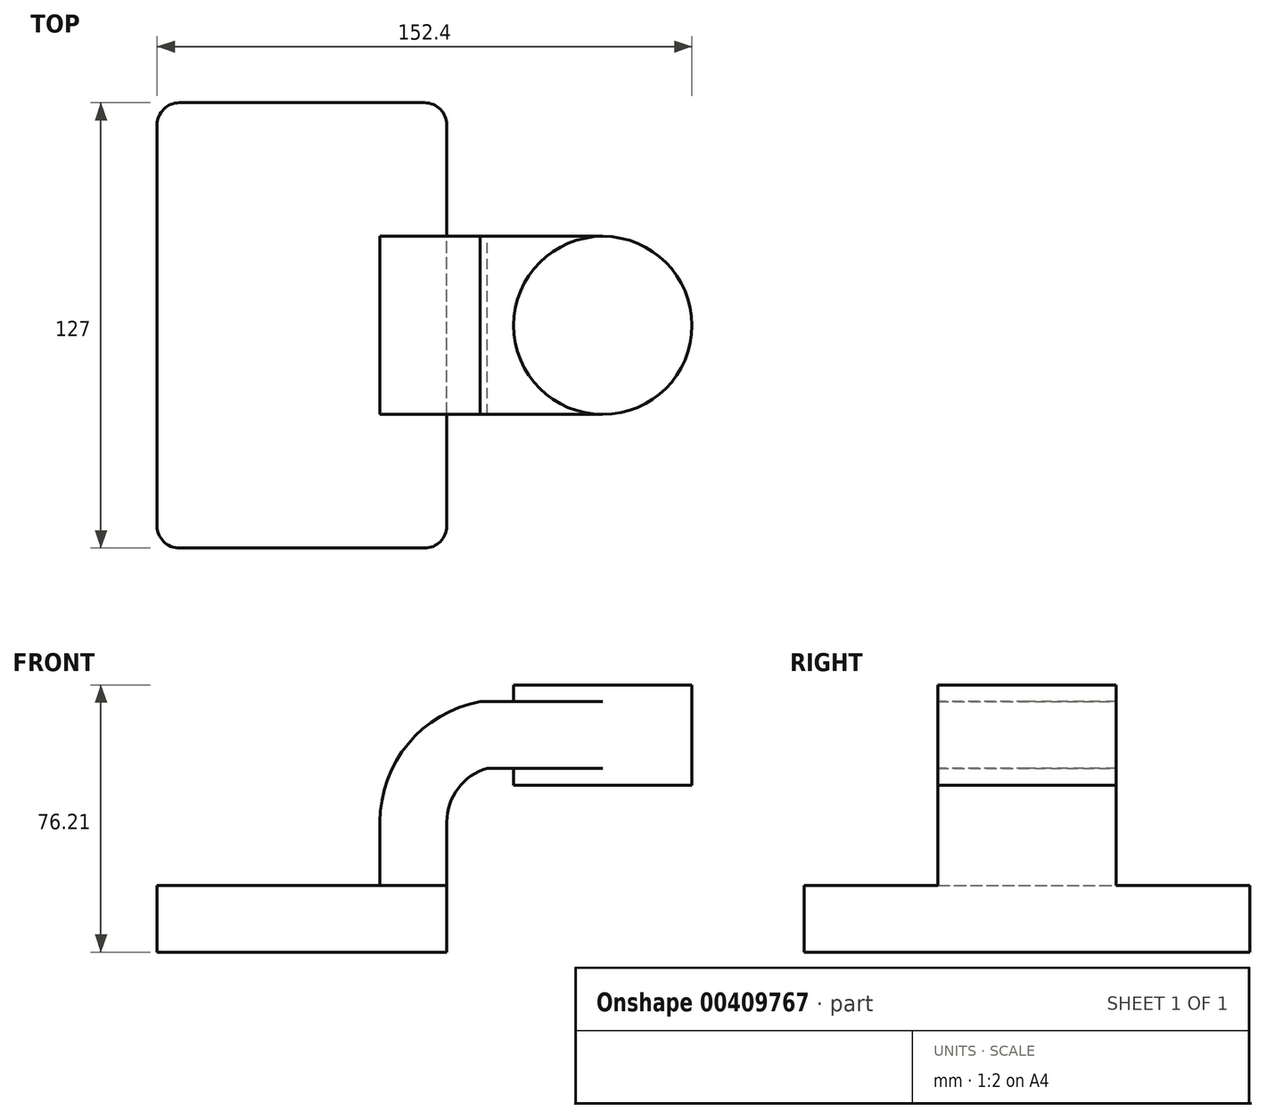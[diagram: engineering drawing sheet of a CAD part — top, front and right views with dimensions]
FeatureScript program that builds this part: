
annotation { "Feature Type Name" : "Feature", "Feature Type Description" : "" }
export const myFeature = defineFeature(function(context is Context, id is Id, definition is map)
    precondition{}
    {
        {
            var Q0;
            Q0=qCreatedBy(makeId("Front.planeOp"),FACE);
            var sketch = newSketch(context, id + "F0", { "sketchPlane" : qUnion([Q0])});
            skLineSegment(sketch, "E0.bottom", {"start": v(41.28, -9.52) * mm, "end": v(-41.28, -9.53) * mm});
            skLineSegment(sketch, "E0.top", {"start": v(41.28, 9.53) * mm, "end": v(-41.28, 9.53) * mm});
            skLineSegment(sketch, "E0.left", {"start": v(41.28, -9.52) * mm, "end": v(41.28, 9.53) * mm});
            skLineSegment(sketch, "E0.right", {"start": v(-41.28, -9.53) * mm, "end": v(-41.28, 9.53) * mm});
            skPoint(sketch, "E0.middle", {"position": v(0, 0) * mm});
            skLineSegment(sketch, "E1.bottom", {"start": v(111.13, 38.1) * mm, "end": v(60.33, 38.1) * mm});
            skLineSegment(sketch, "E1.top", {"start": v(111.13, 66.68) * mm, "end": v(60.33, 66.68) * mm});
            skLineSegment(sketch, "E1.left", {"start": v(111.13, 38.1) * mm, "end": v(111.13, 66.68) * mm});
            skLineSegment(sketch, "E1.right", {"start": v(60.33, 38.1) * mm, "end": v(60.33, 66.68) * mm});
            skPoint(sketch, "E1.middle", {"position": v(85.73, 52.39) * mm});
            skPoint(sketch, "E2.middle", {"position": v(41.28, 9.53) * mm});
            skLineSegment(sketch, "E3", {"start": v(41.28, 9.53) * mm, "end": v(41.28, 27.6) * mm});
            skArc(sketch, "E4", {"start": v(41.27, 27.6) * mm, "mid": v(44.5, 37.18) * mm, "end": v(52.85, 42.88) * mm});
            skLineSegment(sketch, "E5", {"start": v(52.85, 42.88) * mm, "end": v(85.73, 42.88) * mm});
            skLineSegment(sketch, "E6.0", {"start": v(50.74, 61.93) * mm, "end": v(85.73, 61.93) * mm});
            skArc(sketch, "E6.1", {"start": v(22.23, 27.6) * mm, "mid": v(30.28, 49.9) * mm, "end": v(50.74, 61.93) * mm});
            skLineSegment(sketch, "E6.2", {"start": v(22.22, 9.53) * mm, "end": v(22.22, 27.6) * mm});
            skLineSegment(sketch, "E7", {"start": v(85.73, 38.1) * mm, "end": v(85.73, 66.68) * mm});
            skFitSpline(sketch, "E8", {"points": [v(-41.28, 9.52) * mm, v(50.74, 61.93) * mm], "startDerivative": vector(-0.36, 89.6) * mm, "endDerivative": vector(110.06, -0.13) * mm});
            skSolve(sketch);
        }
        {
            var Q0;
            Q0=makeQuery(id+"F0.imprint","IMPRINT",FACE,{"disambiguationData":[TD([[makeQuery(id+"F0.imprint","IMPRINT",EDGE,{"derivedFrom":sQuery(id+"F0.wireOp",EDGE,"E0.bottom")}),-1.0]])]});
            extrude(context, id + "F1", {"entities" : qUnion([Q0]), "endBound" : BoundingType.SYMMETRIC, "depth" : 127 * mm});
        }
        {
            var Q0;
            {var subQ1=sQuery(id+"F0.wireOp",EDGE,"E3");Q0=makeQuery(id+"F0.imprint","IMPRINT",FACE,{"disambiguationData":[TD([[makeQuery(id+"F0.imprint","IMPRINT",EDGE,{"derivedFrom":subQ1}),1.0]])]});}
            var Q1;
            {var subQ0=sQuery(id+"F0.wireOp",EDGE,"E5");var subQ1=sQuery(id+"F0.wireOp",EDGE,"E1.right");var subQ2=makeQuery(id+"F0.imprint","INTERSECT",VERTEX,{"derivedFrom":[subQ1,subQ0]});Q1=makeQuery(id+"F0.imprint","IMPRINT",FACE,{"disambiguationData":[TD([[makeQuery(id+"F0.imprint","IMPRINT",EDGE,{"disambiguationData":[TD([[subQ2,-1.0]])],"derivedFrom":subQ1}),-1.0]])]});}
            extrude(context, id + "F2", {"entities" : qUnion([Q0, Q1]), "operationType" : NewBodyOperationType.ADD, "endBound" : BoundingType.SYMMETRIC, "depth" : 50.8 * mm});
        }
        {
            var Q0;
            Q0=makeQuery(id+"F0.imprint","IMPRINT",FACE,{"disambiguationData":[TD([[makeQuery(id+"F0.imprint","IMPRINT",EDGE,{"derivedFrom":sQuery(id+"F0.wireOp",EDGE,"E6.1")}),1.0]])]});
            extrude(context, id + "F3", {"entities" : qUnion([Q0]), "operationType" : NewBodyOperationType.ADD, "endBound" : BoundingType.SYMMETRIC, "depth" : 15.88 * mm});
        }
        {
            var Q0;
            {var subQ4=sQuery(id+"F0.wireOp",EDGE,"E1.left");Q0=makeQuery(id+"F0.imprint","IMPRINT",FACE,{"disambiguationData":[TD([[makeQuery(id+"F0.imprint","IMPRINT",EDGE,{"derivedFrom":subQ4}),1.0]])]});}
            var Q1;
            Q1=sQuery(id+"F0.wireOp",EDGE,"E7");
            revolve(context, id + "F4", {"operationType" : NewBodyOperationType.ADD, "entities" : qUnion([Q0]), "axis" : qUnion([Q1]), "revolveType" : RevolveType.FULL});
        }
        {
            var Q0;
            Q0=makeQuery(id+"F1.opExtrude","CAP_EDGE",EDGE,{"disambiguationData":[OSD([sQuery(id+"F0.wireOp",EDGE,"E0.right")])],"isStart":false});
            var Q1;
            Q1=makeQuery(id+"F1.opExtrude","CAP_EDGE",EDGE,{"disambiguationData":[OSD([sQuery(id+"F0.wireOp",EDGE,"E0.left")])],"isStart":false});
            var Q2;
            Q2=makeQuery(id+"F1.opExtrude","CAP_EDGE",EDGE,{"disambiguationData":[OSD([sQuery(id+"F0.wireOp",EDGE,"E0.left")])],"isStart":true});
            var Q3;
            Q3=makeQuery(id+"F1.opExtrude","CAP_EDGE",EDGE,{"disambiguationData":[OSD([sQuery(id+"F0.wireOp",EDGE,"E0.right")])],"isStart":true});
            fillet(context, id + "F5", {"entities" : qUnion([Q0, Q1, Q2, Q3]), "radius" : 6.35 * mm, "tangentPropagation" : true, "allowEdgeOverflow" : false});
        }
    });
